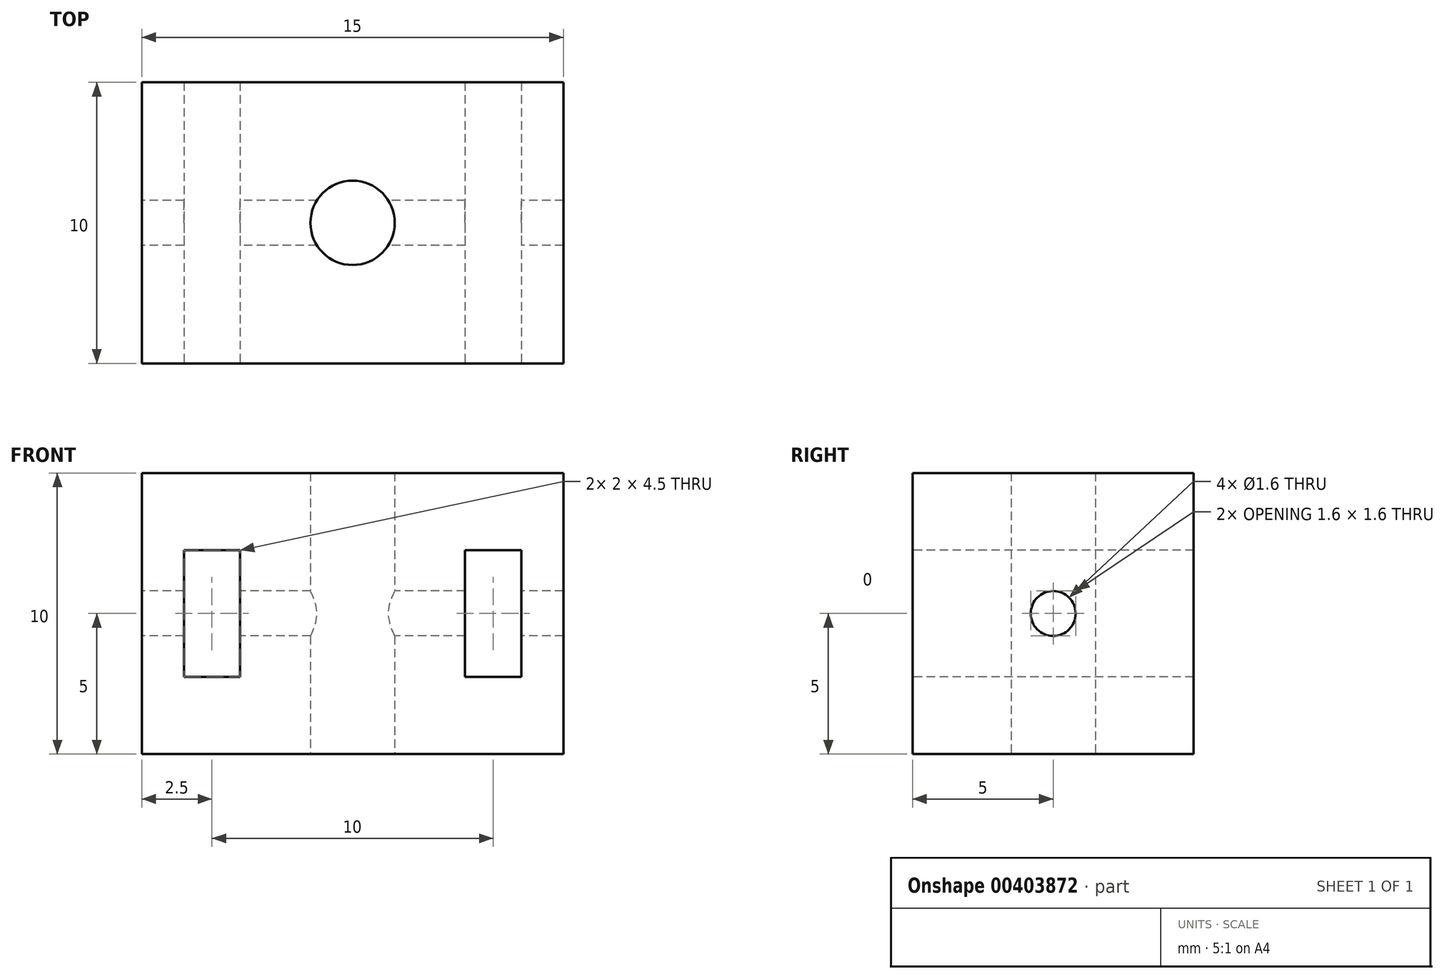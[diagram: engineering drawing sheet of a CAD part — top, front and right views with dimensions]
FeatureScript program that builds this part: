
annotation { "Feature Type Name" : "Feature", "Feature Type Description" : "" }
export const myFeature = defineFeature(function(context is Context, id is Id, definition is map)
    precondition{}
    {
        {
            var Q0;
            Q0=qCreatedBy(makeId("Top.planeOp"),FACE);
            var sketch = newSketch(context, id + "F0", { "sketchPlane" : qUnion([Q0])});
            skLineSegment(sketch, "E0.bottom", {"start": v(7.5, -5) * mm, "end": v(-7.5, -5) * mm});
            skLineSegment(sketch, "E0.top", {"start": v(7.5, 5) * mm, "end": v(-7.5, 5) * mm});
            skLineSegment(sketch, "E0.left", {"start": v(7.5, -5) * mm, "end": v(7.5, 5) * mm});
            skLineSegment(sketch, "E0.right", {"start": v(-7.5, -5) * mm, "end": v(-7.5, 5) * mm});
            skPoint(sketch, "E0.middle", {"position": v(0, 0) * mm});
            skSolve(sketch);
        }
        {
            var Q0;
            Q0 = qSketchRegion(id + "F0", true);
            extrude(context, id + "F1", {"entities" : qUnion([Q0]), "depth" : 10 * mm});
        }
        {
            var Q0;
            Q0=makeQuery(id+"F1.opExtrude","SWEPT_FACE",FACE,{"disambiguationData":[OSD([sQuery(id+"F0.wireOp",EDGE,"E0.bottom")])]});
            var sketch = newSketch(context, id + "F2", { "sketchPlane" : qUnion([Q0])});
            skPoint(sketch, "E1.endSnap0", {"position": v(7.5, 5) * mm});
            skLineSegment(sketch, "E2.bottom", {"start": v(6, 2.75) * mm, "end": v(4, 2.75) * mm});
            skLineSegment(sketch, "E2.top", {"start": v(6, 7.25) * mm, "end": v(4, 7.25) * mm});
            skLineSegment(sketch, "E2.left", {"start": v(6, 2.75) * mm, "end": v(6, 7.25) * mm});
            skLineSegment(sketch, "E2.right", {"start": v(4, 2.75) * mm, "end": v(4, 7.25) * mm});
            skPoint(sketch, "E2.middle", {"position": v(5, 5) * mm});
            skLineSegment(sketch, "E3", {"start": v(0, 10) * mm, "end": v(0, 0) * mm, "construction": true});
            skLineSegment(sketch, "E4.MirrorCS", {"start": v(2, 7.25) * mm, "end": v(4, 7.25) * mm});
            skLineSegment(sketch, "E5.MirrorCS", {"start": v(-4, 2.75) * mm, "end": v(-4, 7.25) * mm});
            skLineSegment(sketch, "E6.MirrorCS", {"start": v(-6, 7.25) * mm, "end": v(-4, 7.25) * mm});
            skLineSegment(sketch, "E7.MirrorCS", {"start": v(-6, 2.75) * mm, "end": v(-6, 7.25) * mm});
            skLineSegment(sketch, "E8.MirrorCS", {"start": v(-6, 2.75) * mm, "end": v(-4, 2.75) * mm});
            skSolve(sketch);
        }
        {
            var Q0;
            Q0=makeQuery(id+"F2.imprint","IMPRINT",FACE,{"disambiguationData":[TD([[makeQuery(id+"F2.imprint","IMPRINT",EDGE,{"derivedFrom":sQuery(id+"F2.wireOp",EDGE,"E5.MirrorCS")}),1.0]])]});
            var Q1;
            Q1=makeQuery(id+"F2.imprint","IMPRINT",FACE,{"disambiguationData":[TD([[makeQuery(id+"F2.imprint","IMPRINT",EDGE,{"derivedFrom":sQuery(id+"F2.wireOp",EDGE,"E2.bottom")}),-1.0]])]});
            extrude(context, id + "F3", {"entities" : qUnion([Q0, Q1]), "operationType" : NewBodyOperationType.REMOVE, "endBound" : BoundingType.UP_TO_NEXT, "oppositeDirection" : true, "depth" : 25 * mm});
        }
        {
            var Q0;
            Q0=makeQuery(id+"F1.opExtrude","CAP_FACE",FACE,{"disambiguationData":[OSD([sQuery(id+"F0.wireOp",EDGE,"E0.bottom"),sQuery(id+"F0.wireOp",EDGE,"E0.top"),sQuery(id+"F0.wireOp",EDGE,"E0.left"),sQuery(id+"F0.wireOp",EDGE,"E0.right")])],"isStart":true});
            var sketch = newSketch(context, id + "F4", { "sketchPlane" : qUnion([Q0])});
            skCircle(sketch, "E9", {"center": v(0, 0) * mm, "radius": 1.5 * mm});
            skSolve(sketch);
        }
        {
            var Q0;
            Q0=makeQuery(id+"F4.imprint","IMPRINT",FACE,{"disambiguationData":[TD([[makeQuery(id+"F4.imprint","IMPRINT",EDGE,{"derivedFrom":sQuery(id+"F4.wireOp",EDGE,"E9")}),1.0]])]});
            extrude(context, id + "F5", {"entities" : qUnion([Q0]), "operationType" : NewBodyOperationType.REMOVE, "oppositeDirection" : true, "depth" : 15 * mm});
        }
        {
            var Q0;
            Q0=makeQuery(id+"F1.opExtrude","SWEPT_FACE",FACE,{"disambiguationData":[OSD([sQuery(id+"F0.wireOp",EDGE,"E0.right")])]});
            var sketch = newSketch(context, id + "F6", { "sketchPlane" : qUnion([Q0])});
            skLineSegment(sketch, "E10", {"start": v(5, 5) * mm, "end": v(0, 5) * mm, "construction": true});
            skCircle(sketch, "E11", {"center": v(0, 5) * mm, "radius": 0.8 * mm});
            skSolve(sketch);
        }
        {
            var Q0;
            Q0=makeQuery(id+"F6.imprint","IMPRINT",FACE,{"disambiguationData":[TD([[makeQuery(id+"F6.imprint","IMPRINT",EDGE,{"derivedFrom":sQuery(id+"F6.wireOp",EDGE,"E11")}),1.0]])]});
            var Q1;
            Q1=makeQuery(id+"F1.opExtrude","SWEPT_FACE",FACE,{"disambiguationData":[OSD([sQuery(id+"F0.wireOp",EDGE,"E0.left")])]});
            extrude(context, id + "F7", {"entities" : qUnion([Q0]), "operationType" : NewBodyOperationType.REMOVE, "endBound" : BoundingType.UP_TO_SURFACE, "oppositeDirection" : true, "endBoundEntityFace" : qUnion([Q1]), "depth" : 25 * mm});
        }
    });
